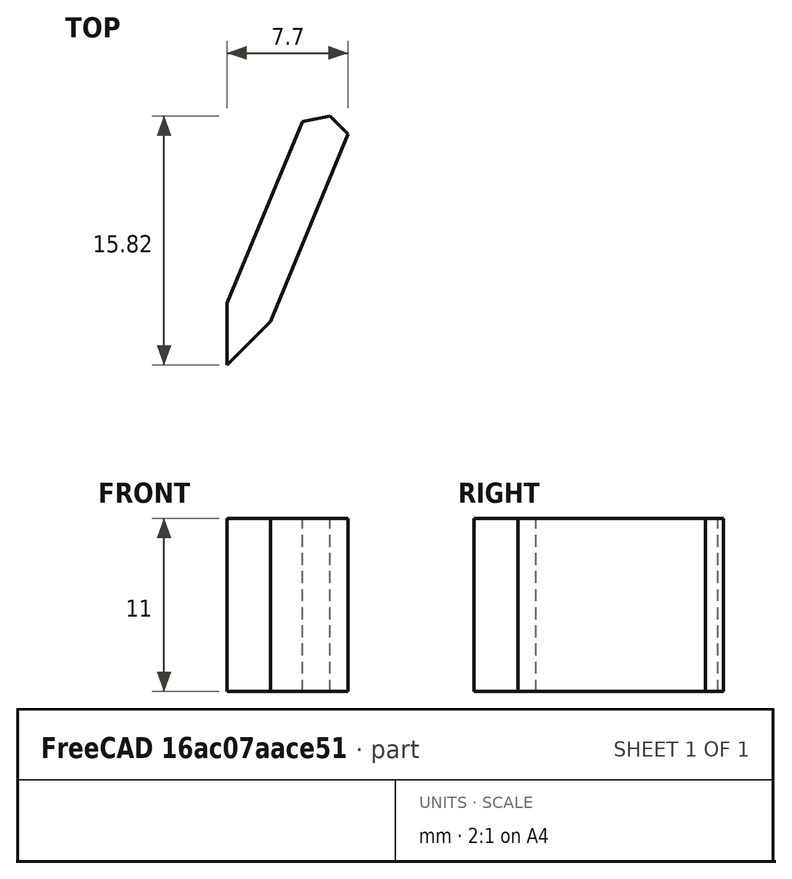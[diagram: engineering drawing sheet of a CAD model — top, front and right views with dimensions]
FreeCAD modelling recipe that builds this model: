
FCSTD DOCUMENT  (FreeCAD 0.21R33694 (Git))
Label: kumiko_inlay_hindge
License: All rights reserved
LicenseURL: https://en.wikipedia.org/wiki/All_rights_reserved
objects: Sketcher::SketchObject×1, PartDesign::Pad×1, PartDesign::Body×1, App::Link×1
note: 4 computed .brp shape members not serialized (recipe doc carries the construction recipe); baked Part::Feature solids carry a one-line shape summary decoded from their .brp
EXTERNAL_REF file=../../master_kumiko_box.FCStd obj=Spreadsheet

FEATURE [Sketcher::SketchObject] Sketch097  label="hindge_drawing"
  FullyConstrained = true
  MapMode = 5
  Support = -> [XY_Plane083]
  expr: Constraints[0] = 0
  expr: Constraints[11] = <<SpreadSheet>>.kumiko_grid_size * (1 - 1 / sqrt(2)) - 1 / 2 * <<SpreadSheet>>.kumiko_thickness
  expr: Constraints[12] = <<SpreadSheet>>.kumiko_grid_size / sqrt(2) - <<SpreadSheet>>.kumiko_thickness * (1 + 1 / sqrt(2)) * 1 / sqrt(2)
  expr: Constraints[18] = 45
  expr: Constraints[1] = 0
  expr: Constraints[2] = 135 °
  expr: Constraints[4] = 2 * 22.5
  expr: Constraints[6] = <<SpreadSheet>>.kumiko_thickness
  expr: Constraints[7] = (<<SpreadSheet>>.kumiko_grid_size - <<SpreadSheet>>.kumiko_thickness * (1 + sqrt(2) + 1 / sqrt(2 - sqrt(2)))) * 1 / sqrt(2)
  expr: Constraints[8] = (<<SpreadSheet>>.kumiko_grid_size - <<SpreadSheet>>.kumiko_thickness * (1 + sqrt(2) + 1 / sqrt(2 - sqrt(2)))) * (1 - 1 / sqrt(2))
  sketch-geometry (8):
    g0: LineSegment StartX=0 StartY=0 StartZ=0 EndX=2.77164 EndY=2.77164 EndZ=0
    g1: LineSegment StartX=0 StartY=0 StartZ=0 EndX=-2e-16 EndY=3.91969 EndZ=0
    g2: GeomPoint X=4.78519 Y=15.4722 Z=0
    g3: LineSegment StartX=-2e-16 StartY=3.91969 StartZ=0 EndX=4.78519 EndY=15.4722 EndZ=0
    g4: GeomPoint X=6.55456 Y=15.8241 Z=0
    g5: LineSegment StartX=4.78519 StartY=15.4722 StartZ=0 EndX=6.55456 EndY=15.8241 EndZ=0
    g6: LineSegment StartX=2.77164 StartY=2.77164 StartZ=0 EndX=7.70261 EndY=14.6761 EndZ=0
    g7: LineSegment StartX=6.55456 StartY=15.8241 StartZ=0 EndX=7.70261 EndY=14.6761 EndZ=0
  constraints (20):
    c: DistanceX(g-1,g0) = 0
    c: DistanceY(g-1,g0) = 0
    c: Angle(g0,g-1) = 2.35619
    c: Coincident(g1,g0)
    c: Angle(g0,g1) = 0.785398
    c: Equal(g1,g0)
    c: Distance(g0,g1) = 3
    c: DistanceY(g1,g2) = 11.5525
    c: DistanceX(g1,g2) = 4.78519
    c: Coincident(g3,g1)
    c: Coincident(g3,g2)
    c: DistanceX(g0,g4) = 6.55456
    c: DistanceY(g0,g4) = 15.8241
    c: Coincident(g5,g3)
    c: Coincident(g5,g4)
    c: Coincident(g6,g0)
    c: Parallel(g3,g6)
    c: Coincident(g7,g5)
    c: Angle(g7,g-1) = 0.785398
    c: Coincident(g7,g6)
FEATURE [PartDesign::Pad] Pad049  label="hindge_extrude"
  Direction = (0,0,1)
  Length = 11
  Length2 = 10
  Profile = -> Sketch097
  ReferenceAxis = -> Sketch097 [N_Axis]
  Type = 0
  expr: Length = <<SpreadSheet>>.kumiko_hight
FEATURE [PartDesign::Body] Body062  label="hindge_body"
  Group = -> [Sketch097,Pad049]
  Origin = -> Origin083
  Tip = -> Pad049
  expr: .Placement.Base.z = 0
FEATURE [App::Link] Link  label="SpreadSheet"
  LinkedObject = -> <external ../../master_kumiko_box.FCStd>#Spreadsheet
